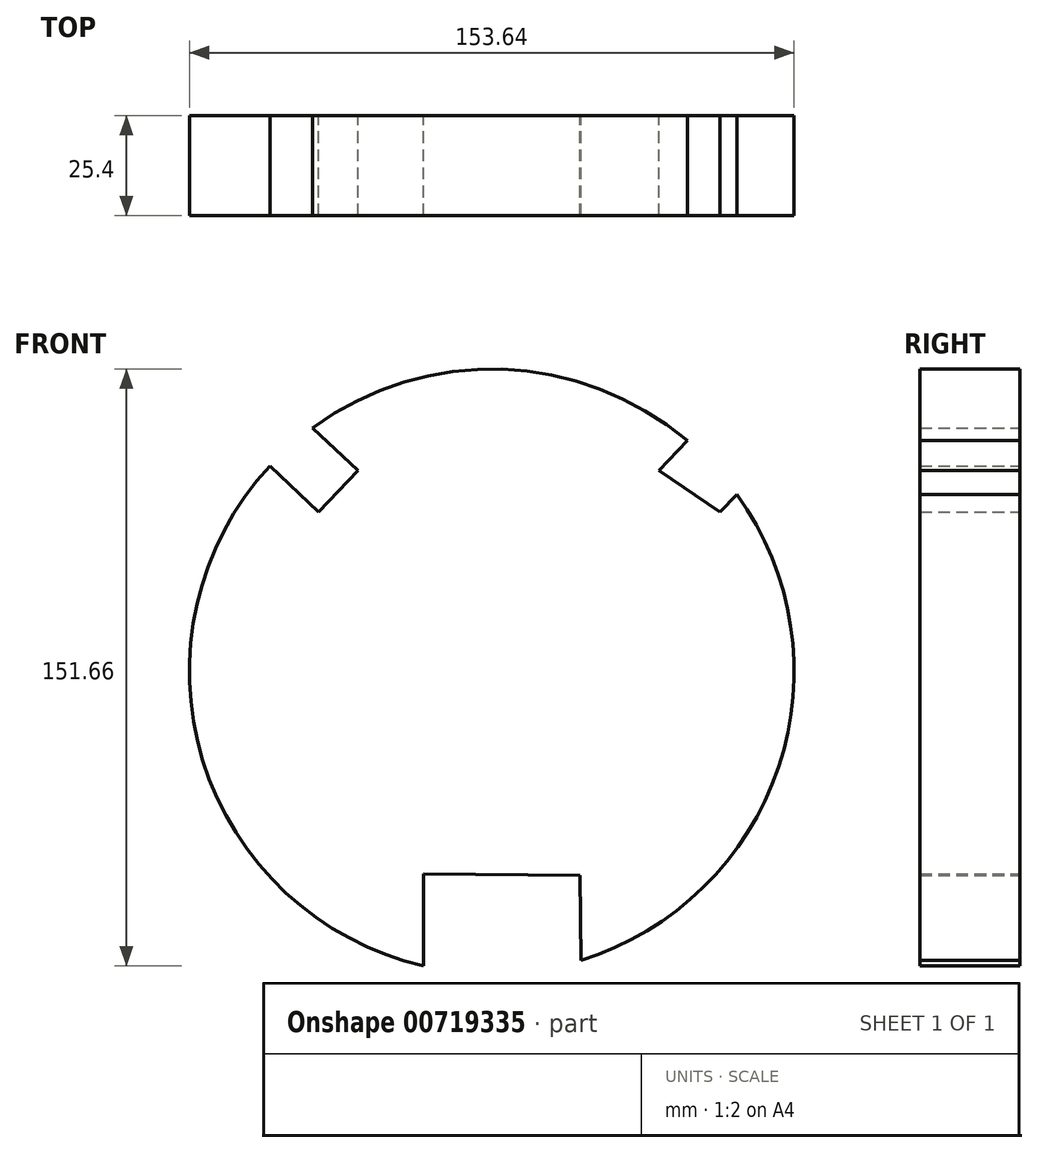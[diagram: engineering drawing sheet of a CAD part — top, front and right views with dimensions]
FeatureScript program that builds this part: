
annotation { "Feature Type Name" : "Feature", "Feature Type Description" : "" }
export const myFeature = defineFeature(function(context is Context, id is Id, definition is map)
    precondition{}
    {
        {
            var Q0;
            Q0=qCreatedBy(makeId("Front.planeOp"),FACE);
            var sketch = newSketch(context, id + "F0", { "sketchPlane" : qUnion([Q0])});
            skCircle(sketch, "E0", {"center": v(0, 0) * mm, "radius": 76.82 * mm});
            skLineSegment(sketch, "E1", {"start": v(-63.35, 58.77) * mm, "end": v(-44.01, 40.45) * mm});
            skLineSegment(sketch, "E2", {"start": v(-44.01, 40.45) * mm, "end": v(-34, 51.01) * mm});
            skLineSegment(sketch, "E3", {"start": v(-34, 51.01) * mm, "end": v(-54.64, 70.56) * mm});
            skLineSegment(sketch, "E4", {"start": v(-54.64, 70.56) * mm, "end": v(-63.35, 58.77) * mm});
            skLineSegment(sketch, "E5", {"start": v(42.49, 51.01) * mm, "end": v(61, 70.56) * mm});
            skLineSegment(sketch, "E6", {"start": v(61, 70.56) * mm, "end": v(73.45, 58.77) * mm});
            skLineSegment(sketch, "E7", {"start": v(73.45, 56.73) * mm, "end": v(58.03, 40.45) * mm});
            skLineSegment(sketch, "E8", {"start": v(58.03, 40.45) * mm, "end": v(42.49, 51.01) * mm});
            skLineSegment(sketch, "E9", {"start": v(73.45, 58.77) * mm, "end": v(73.45, 56.73) * mm});
            skLineSegment(sketch, "E10", {"start": v(-17.3, -51.39) * mm, "end": v(-17.3, -77.08) * mm});
            skLineSegment(sketch, "E11", {"start": v(-17.3, -77.08) * mm, "end": v(22.76, -76.48) * mm});
            skLineSegment(sketch, "E12", {"start": v(22.76, -76.48) * mm, "end": v(22.39, -51.8) * mm});
            skLineSegment(sketch, "E13", {"start": v(22.39, -51.8) * mm, "end": v(-17.3, -51.39) * mm});
            skSolve(sketch);
        }
        {
            var Q0;
            {var subQ5=sQuery(id+"F0.wireOp",EDGE,"E2");Q0=makeQuery(id+"F0.imprint","IMPRINT",FACE,{"disambiguationData":[TD([[makeQuery(id+"F0.imprint","IMPRINT",EDGE,{"derivedFrom":subQ5}),-1.0]])]});}
            extrude(context, id + "F1", {"entities" : qUnion([Q0]), "depth" : 25.4 * mm, "offsetDistance" : 25.4 * mm});
        }
    });
